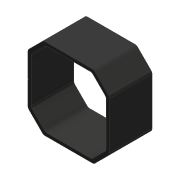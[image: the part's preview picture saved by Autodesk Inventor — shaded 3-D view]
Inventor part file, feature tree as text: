
AUTODESK INVENTOR PART (.ipt)
format: ipt  version: 2018 (Build 220112000, 112)  size: 175,616 bytes
history: native  units: mm
features: sketch x4, extrude x3, fillet x2, chamfer x1, projected_geometry x1
ambient origin geometry x8: Origin, YZ Plane, XZ Plane, XY Plane, X Axis, Y Axis, Z Axis, Center Point
bodies: Solid1 (feature_tree)
feature tree (11):
  extrude  "Extrusion1"  Depth=42.0mm
  chamfer  "Chamfer1"  Distance=22.0mm
  fillet  "Fillet1"  Radius=2.0mm
  extrude  "Extrusion2"  Depth=20.0mm
  extrude  "Extrusion3"  Depth=10.0mm
  sketch  "Sketch6"  dims[d19=10.0mm d20=10.0mm d21=0.001mm d22=0.0mm d23=2.0mm]
  fillet  "Fillet2"  Radius=0.001mm
  sketch  "Sketch1"  dims[d0=42.0mm d1=42.0mm d2=22.0mm d3=0.0mm]
  sketch  "Sketch4"  dims[d4=8.0mm d5=2.0mm d6=45.0deg d7=2.0mm]
  projected_geometry  "Projected Loop2"
  sketch  "Sketch5"  dims[d8=22.0mm d9=0.0mm d18=20.0mm]
